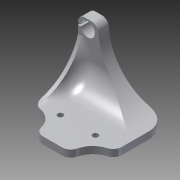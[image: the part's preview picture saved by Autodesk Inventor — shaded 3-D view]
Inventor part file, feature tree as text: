
AUTODESK INVENTOR PART (.ipt)
format: ipt  version: 2015 SP1 (Build 190203100, 203)  size: 328,192 bytes
history: native  units: mm
features: extrude x9, sketch x9, fillet x6, projected_geometry x5, reference x5, hole x2, mirror x1
ambient origin geometry x8: Origin, YZ Plane, XZ Plane, XY Plane, X Axis, Y Axis, Z Axis, Center Point
bodies: Solid2 (feature_tree)
feature tree (37):
  extrude  "back plate Extrusion2"  Depth=18.0mm
  extrude  "Extrusion3"  Depth=4.0mm
  extrude  "Extrusion6"  Depth=8.0mm
  extrude  "Extrusion7"  Depth=11.5mm TaperAngle=0.0deg
  hole  "Hole4"  [1 undecoded]
  extrude  "Extrusion8"  Depth=20.35mm
  extrude  "Extrusion9"  Depth=1.0mm
  fillet  "Fillet4"  Radius=6.0mm
  extrude  "Extrusion10"  Depth=15.85mm TaperAngle=0.0deg
  extrude  "Extrusion12"  Depth=4.0mm
  extrude  "Extrusion13"  Depth=5.0mm TaperAngle=0.0deg
  fillet  "Fillet13"  Radius=5.25mm
  fillet  "Fillet14"  Radius=30.0mm
  fillet  "Fillet15"  Radius=2.0mm
  fillet  "Fillet16"  Radius=30.0mm
  fillet  "Fillet17"  Radius=13.0mm
  hole  "Hole5"  [1 undecoded]
  mirror  "Mirror1"
  sketch  "Sketch4"  dims[d21=4.0mm d22=0.0mm d31=18.0mm]
  projected_geometry  "Projected Loop1"
  sketch  "Sketch9"  dims[d32=4.0mm d33=4.0mm]
  reference  "Reference1"
  reference  "Reference2"
  sketch  "Sketch11"  dims[d34=17.0mm d35=8.0mm]
  reference  "Reference3"
  sketch  "Sketch12"  dims[d36=8.0mm d44=11.5mm d45=0.0mm]
  sketch  "Sketch13"  dims[d58=4.0mm d59=6.0mm d60=0.0mm]
  projected_geometry  "Projected Loop2"
  sketch  "Sketch14"  dims[d63=5.5mm d64=20.35mm]
  projected_geometry  "Projected Loop3"
  sketch  "Sketch16"  dims[d65=6.0mm d66=0.0mm]
  projected_geometry  "Projected Loop5"
  sketch  "Sketch17"  dims[d67=8.0mm d68=6.0mm d69=4.0mm d70=2.0mm d71=90.0deg d72=8.0mm d73=20.594885mm d74=1.0mm d75=6.0mm]
  projected_geometry  "Projected Loop6"
  sketch  "Sketch19"  dims[d76=6.0mm d77=0.0mm d78=15.85mm d79=0.0mm d80=4.0mm d85=5.0mm d86=0.0mm d94=5.25mm d95=0.0mm d96=30.0mm d97=2.0mm d98=0.0mm d101=30.0mm d102=13.0mm d103=12.0mm d104=5.0mm d105=7.0mm d106=3.2mm d107=6.0mm d108=4.0mm d109=2.0mm d110=90.0deg d111=8.0mm d112=20.594885mm]
  reference  "Reference4"
  reference  "Reference5"
note: 2 required parameter values undecoded (feature->parameter linkage not recoverable at this tier; creation-order binding heuristic only, values carry confidence <= 0.55)
